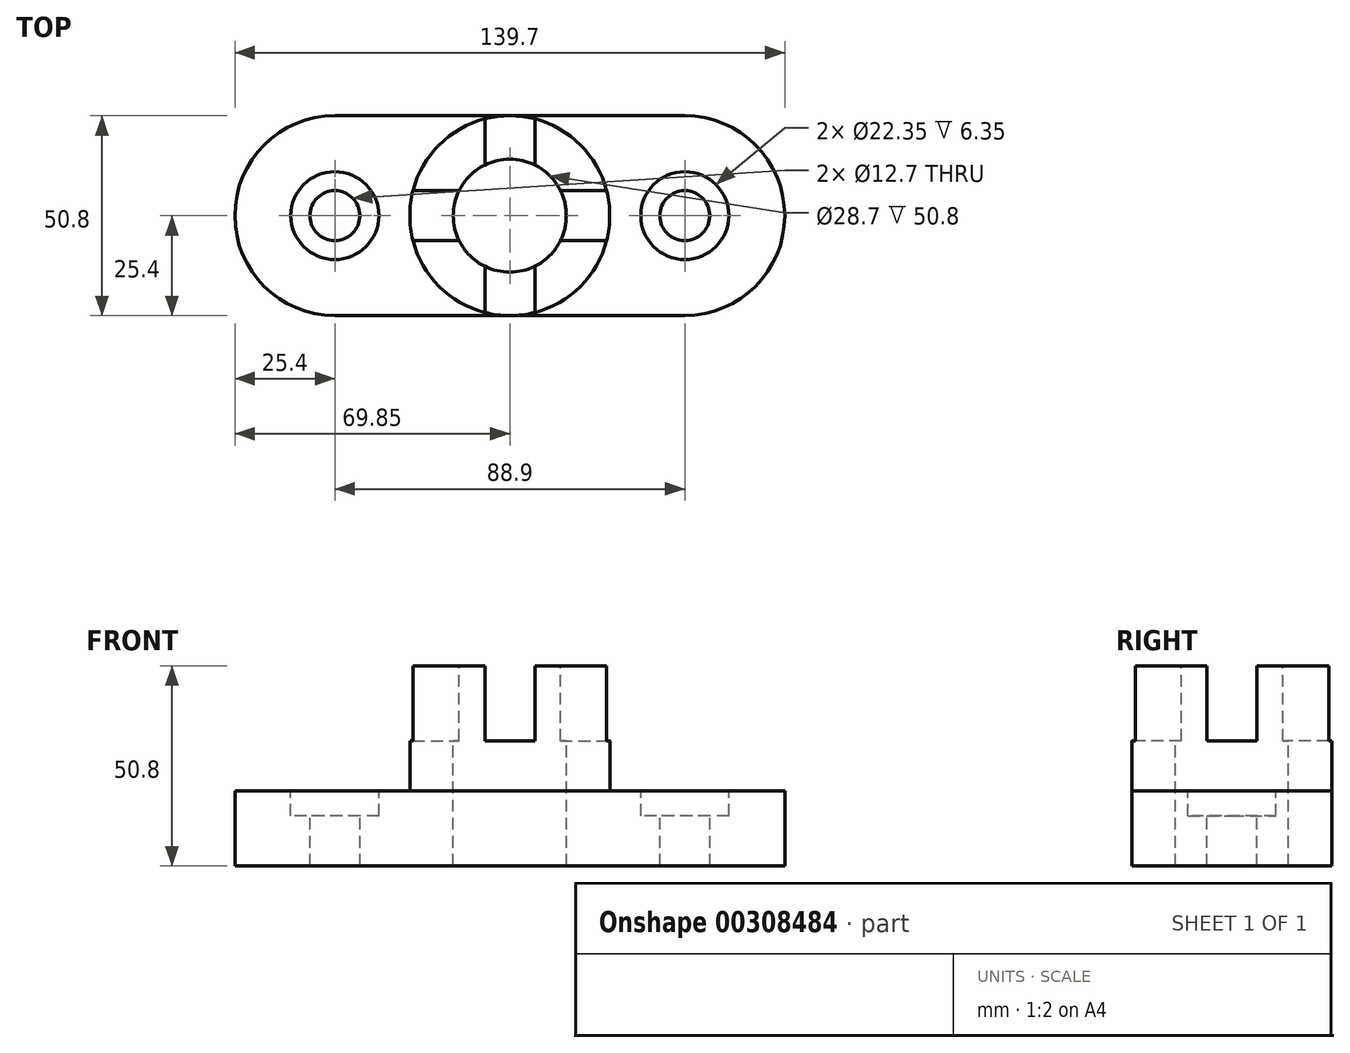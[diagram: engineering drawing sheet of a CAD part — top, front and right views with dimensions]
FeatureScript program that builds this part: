
annotation { "Feature Type Name" : "Feature", "Feature Type Description" : "" }
export const myFeature = defineFeature(function(context is Context, id is Id, definition is map)
    precondition{}
    {
        {
            var Q0;
            Q0=qCreatedBy(makeId("Top.planeOp"),FACE);
            var sketch = newSketch(context, id + "F0", { "sketchPlane" : qUnion([Q0])});
            skArc(sketch, "E0", {"start": v(0, 25.4) * mm, "mid": v(-25.4, 0) * mm, "end": v(0, -25.4) * mm});
            skArc(sketch, "E1", {"start": v(88.9, -25.4) * mm, "mid": v(114.3, 0) * mm, "end": v(88.9, 25.4) * mm});
            skLineSegment(sketch, "E2", {"start": v(0, 25.4) * mm, "end": v(88.9, 25.4) * mm});
            skLineSegment(sketch, "E3", {"start": v(88.9, -25.4) * mm, "end": v(0, -25.4) * mm});
            skSolve(sketch);
        }
        {
            var Q0;
            Q0 = qSketchRegion(id + "F0", true);
            extrude(context, id + "F1", {"entities" : qUnion([Q0]), "depth" : 19.05 * mm});
        }
        {
            var Q0;
            Q0=makeQuery(id+"F1.opExtrude","CAP_FACE",FACE,{"disambiguationData":[OSD([sQuery(id+"F0.wireOp",EDGE,"E0"),sQuery(id+"F0.wireOp",EDGE,"E1"),sQuery(id+"F0.wireOp",EDGE,"E2"),sQuery(id+"F0.wireOp",EDGE,"E3")])],"isStart":false});
            var sketch = newSketch(context, id + "F2", { "sketchPlane" : qUnion([Q0])});
            skCircle(sketch, "E4", {"center": v(0, 0) * mm, "radius": 11.18 * mm});
            skCircle(sketch, "E5", {"center": v(88.9, 0) * mm, "radius": 11.18 * mm});
            skSolve(sketch);
        }
        {
            var Q0;
            Q0 = qSketchRegion(id + "F2", true);
            extrude(context, id + "F3", {"entities" : qUnion([Q0]), "operationType" : NewBodyOperationType.REMOVE, "oppositeDirection" : true, "depth" : 6.35 * mm});
        }
        {
            var Q0;
            Q0=makeQuery(id+"F3.boolean.opBoolean","COPY",FACE,{"derivedFrom":makeQuery(id+"F3.opExtrude","CAP_FACE",FACE,{"disambiguationData":[OSD([sQuery(id+"F2.wireOp",EDGE,"E4")])],"isStart":false})});
            var sketch = newSketch(context, id + "F4", { "sketchPlane" : qUnion([Q0])});
            skCircle(sketch, "E6", {"center": v(0, 0) * mm, "radius": 6.35 * mm});
            skSolve(sketch);
        }
        {
            var Q0;
            Q0 = qSketchRegion(id + "F4", true);
            extrude(context, id + "F5", {"entities" : qUnion([Q0]), "operationType" : NewBodyOperationType.REMOVE, "oppositeDirection" : true, "depth" : 25.4 * mm});
        }
        {
            var Q0;
            Q0=makeQuery(id+"F3.boolean.opBoolean","COPY",FACE,{"derivedFrom":makeQuery(id+"F3.opExtrude","CAP_FACE",FACE,{"disambiguationData":[OSD([sQuery(id+"F2.wireOp",EDGE,"E5")])],"isStart":false})});
            var sketch = newSketch(context, id + "F6", { "sketchPlane" : qUnion([Q0])});
            skCircle(sketch, "E7", {"center": v(88.9, 0) * mm, "radius": 6.35 * mm});
            skSolve(sketch);
        }
        {
            var Q0;
            Q0 = qSketchRegion(id + "F6", true);
            extrude(context, id + "F7", {"entities" : qUnion([Q0]), "operationType" : NewBodyOperationType.REMOVE, "oppositeDirection" : true, "depth" : 25.4 * mm});
        }
        {
            var Q0;
            Q0=makeQuery(id+"F1.opExtrude","CAP_FACE",FACE,{"disambiguationData":[OSD([sQuery(id+"F0.wireOp",EDGE,"E0"),sQuery(id+"F0.wireOp",EDGE,"E1"),sQuery(id+"F0.wireOp",EDGE,"E2"),sQuery(id+"F0.wireOp",EDGE,"E3")])],"isStart":false});
            var sketch = newSketch(context, id + "F8", { "sketchPlane" : qUnion([Q0])});
            skCircle(sketch, "E8", {"center": v(44.45, 0) * mm, "radius": 25.4 * mm});
            skSolve(sketch);
        }
        {
            var Q0;
            Q0 = qSketchRegion(id + "F8", true);
            extrude(context, id + "F9", {"entities" : qUnion([Q0]), "operationType" : NewBodyOperationType.ADD, "depth" : 31.75 * mm});
        }
        {
            var Q0;
            Q0=makeQuery(id+"F9.opExtrude","CAP_FACE",FACE,{"disambiguationData":[OSD([sQuery(id+"F8.wireOp",EDGE,"E8")])],"isStart":false});
            var sketch = newSketch(context, id + "F10", { "sketchPlane" : qUnion([Q0])});
            skCircle(sketch, "E9", {"center": v(44.45, 0) * mm, "radius": 14.35 * mm});
            skSolve(sketch);
        }
        {
            var Q0;
            Q0 = qSketchRegion(id + "F10", true);
            extrude(context, id + "F11", {"entities" : qUnion([Q0]), "operationType" : NewBodyOperationType.REMOVE, "oppositeDirection" : true, "depth" : 50.8 * mm});
        }
        {
            var Q0;
            Q0=makeQuery(id+"F1.opExtrude","SWEPT_FACE",FACE,{"disambiguationData":[OSD([sQuery(id+"F0.wireOp",EDGE,"E3")])]});
            var sketch = newSketch(context, id + "F12", { "sketchPlane" : qUnion([Q0])});
            skLineSegment(sketch, "E10", {"start": v(19.05, 19.05) * mm, "end": v(19.05, 50.8) * mm});
            skLineSegment(sketch, "E11", {"start": v(69.85, 50.8) * mm, "end": v(69.85, 19.05) * mm});
            skLineSegment(sketch, "E12", {"start": v(38.1, 50.8) * mm, "end": v(50.8, 50.8) * mm});
            skLineSegment(sketch, "E13", {"start": v(50.8, 50.8) * mm, "end": v(50.8, 31.75) * mm});
            skLineSegment(sketch, "E14", {"start": v(50.8, 31.75) * mm, "end": v(38.1, 31.75) * mm});
            skLineSegment(sketch, "E15", {"start": v(38.1, 31.75) * mm, "end": v(38.1, 50.8) * mm});
            skSolve(sketch);
        }
        {
            var Q0;
            Q0 = qSketchRegion(id + "F12", true);
            extrude(context, id + "F13", {"entities" : qUnion([Q0]), "operationType" : NewBodyOperationType.REMOVE, "oppositeDirection" : true, "depth" : 50.8 * mm});
        }
        {
            var Q0;
            Q0=qCreatedBy(makeId("Right.planeOp"),FACE);
            cPlane(context, id + "F14", {"entities" : qUnion([Q0]), "cplaneType" : CPlaneType.OFFSET, "offset" : 69.85 * mm, "width" : 152.4 * mm, "height" : 152.4 * mm});
        }
        {
            var Q0;
            Q0=qCreatedBy(id+"F14.planeOp",FACE);
            var sketch = newSketch(context, id + "F15", { "sketchPlane" : qUnion([Q0])});
            skLineSegment(sketch, "E16", {"start": v(-25.4, 19.05) * mm, "end": v(-25.4, 31.75) * mm});
            skLineSegment(sketch, "E17", {"start": v(25.4, 31.75) * mm, "end": v(25.4, 19.05) * mm});
            skLineSegment(sketch, "E18", {"start": v(-6.35, 50.8) * mm, "end": v(-6.35, 31.75) * mm});
            skLineSegment(sketch, "E19", {"start": v(-6.35, 31.75) * mm, "end": v(6.35, 31.75) * mm});
            skLineSegment(sketch, "E20", {"start": v(6.35, 31.75) * mm, "end": v(6.35, 50.8) * mm});
            skLineSegment(sketch, "E21", {"start": v(6.35, 50.8) * mm, "end": v(-6.35, 50.8) * mm});
            skSolve(sketch);
        }
        {
            var Q0;
            Q0 = qSketchRegion(id + "F15", true);
            extrude(context, id + "F16", {"entities" : qUnion([Q0]), "operationType" : NewBodyOperationType.REMOVE, "oppositeDirection" : true, "depth" : 50.8 * mm});
        }
    });
